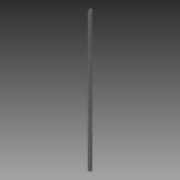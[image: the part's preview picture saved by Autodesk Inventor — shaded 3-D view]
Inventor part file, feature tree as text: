
AUTODESK INVENTOR PART (.ipt)
format: ipt  version: 2015 SP1 (Build 190203100, 203)  size: 82,944 bytes
history: native  units: mm
features: other x3, sketch x3
ambient origin geometry x8: Origin, YZ Plane, XZ Plane, XY Plane, X Axis, Y Axis, Z Axis, Center Point
bodies: Solid1 (feature_tree)
feature tree (6):
  other  "Poutre.ipt"
  other  "Solid1::Poutre.ipt"
  other  "TaggingFeature1"
  sketch  "Sketch1"  dims[d0=10.0mm]
  sketch  "Sketch2"
  sketch  "Sketch3"
